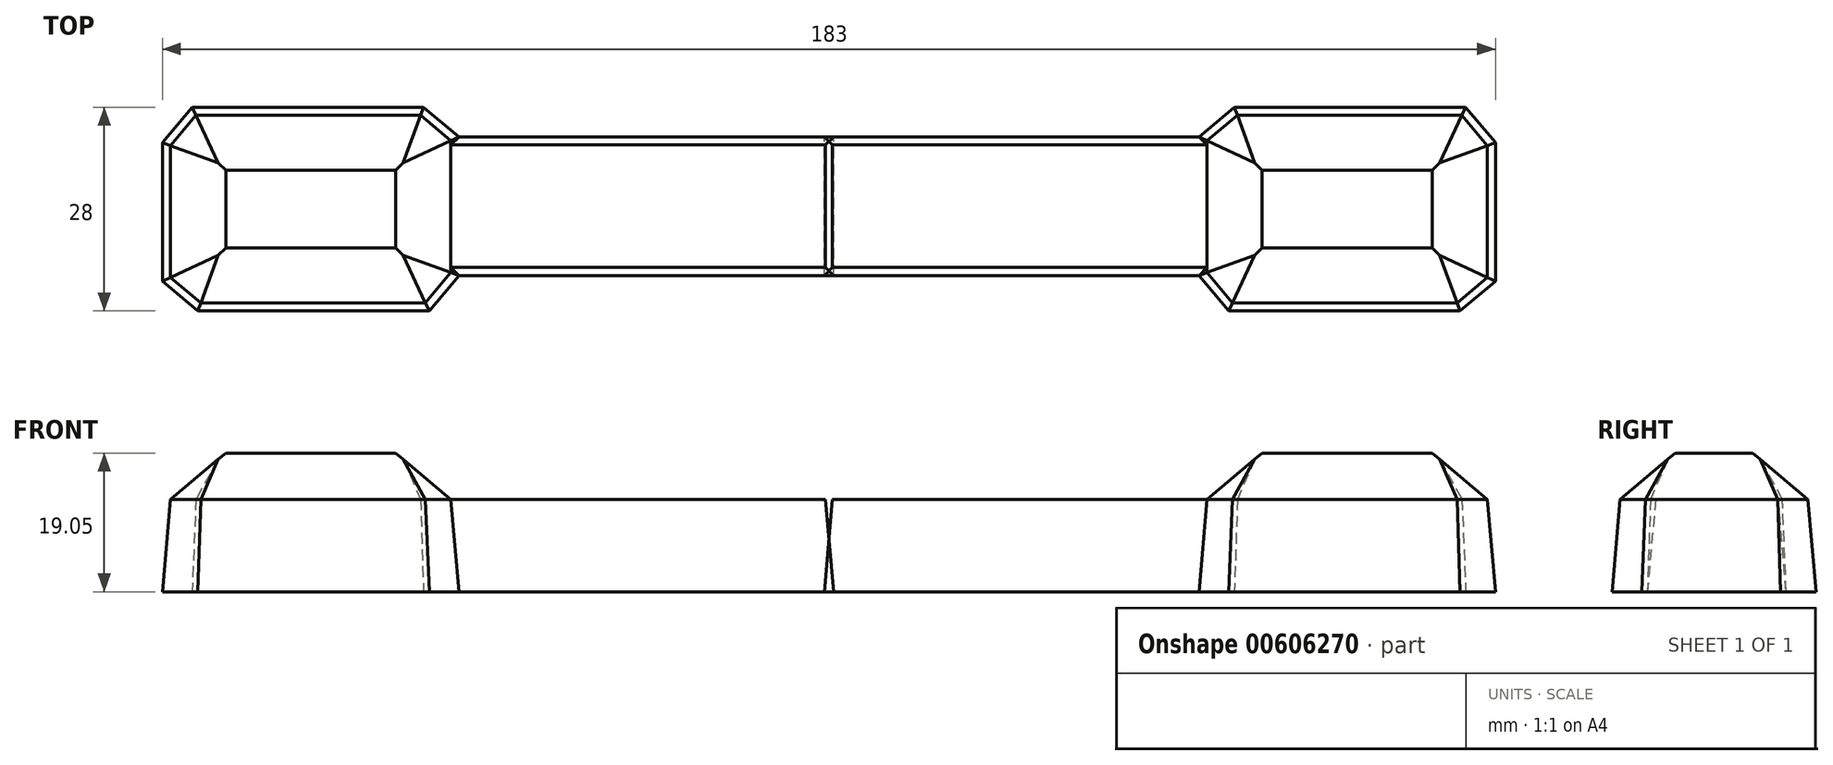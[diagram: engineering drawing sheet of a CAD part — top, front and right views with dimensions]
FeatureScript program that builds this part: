
annotation { "Feature Type Name" : "Feature", "Feature Type Description" : "" }
export const myFeature = defineFeature(function(context is Context, id is Id, definition is map)
    precondition{}
    {
        {
            var Q0;
            Q0=qCreatedBy(makeId("Top.planeOp"),FACE);
            var sketch = newSketch(context, id + "F0", { "sketchPlane" : qUnion([Q0])});
            skPoint(sketch, "E0.middle", {"position": v(0, 0) * mm});
            skLineSegment(sketch, "E1", {"start": v(50.8, 9.53) * mm, "end": v(50.8, -9.52) * mm});
            skLineSegment(sketch, "E2", {"start": v(50.8, 9.52) * mm, "end": v(55.66, 13.6) * mm});
            skLineSegment(sketch, "E3", {"start": v(50.8, -9.52) * mm, "end": v(54.88, -14.39) * mm});
            skLineSegment(sketch, "E4", {"start": v(54.88, -14.39) * mm, "end": v(86.63, -14.39) * mm});
            skLineSegment(sketch, "E5", {"start": v(55.66, 13.6) * mm, "end": v(87.41, 13.6) * mm});
            skLineSegment(sketch, "E6", {"start": v(87.41, 13.6) * mm, "end": v(91.5, 8.74) * mm});
            skLineSegment(sketch, "E7", {"start": v(86.63, -14.39) * mm, "end": v(91.5, -10.3) * mm});
            skLineSegment(sketch, "E8", {"start": v(91.5, 8.74) * mm, "end": v(91.5, -10.3) * mm});
            skLineSegment(sketch, "E9", {"start": v(50.8, 9.53) * mm, "end": v(57.13, 9.53) * mm});
            skLineSegment(sketch, "E10", {"start": v(57.13, 9.53) * mm, "end": v(57.13, -9.53) * mm});
            skLineSegment(sketch, "E11", {"start": v(57.13, -9.53) * mm, "end": v(50.8, -9.53) * mm});
            skLineSegment(sketch, "E12", {"start": v(-0.62, 9.53) * mm, "end": v(-0.62, -9.53) * mm});
            skLineSegment(sketch, "E13", {"start": v(-0.62, 9.53) * mm, "end": v(50.8, 9.53) * mm});
            skLineSegment(sketch, "E14", {"start": v(-0.62, -9.52) * mm, "end": v(50.8, -9.52) * mm});
            skSolve(sketch);
        }
        {
            var Q0;
            Q0=makeQuery(id+"F0.imprint","IMPRINT",FACE,{"disambiguationData":[TD([[makeQuery(id+"F0.imprint","IMPRINT",EDGE,{"derivedFrom":sQuery(id+"F0.wireOp",EDGE,"LX4vih2L-8PL2-zWTP-tvqg-00dXrwP9e0R8")}),-1.0]])]});
            var Q1;
            Q1=makeQuery(id+"F0.imprint","IMPRINT",FACE,{"disambiguationData":[TD([[makeQuery(id+"F0.imprint","IMPRINT",EDGE,{"derivedFrom":sQuery(id+"F0.wireOp",EDGE,"E1")}),1.0]])]});
            var Q2;
            Q2=makeQuery(id+"F0.imprint","IMPRINT",FACE,{"disambiguationData":[TD([[makeQuery(id+"F0.imprint","IMPRINT",EDGE,{"derivedFrom":sQuery(id+"F0.wireOp",EDGE,"E1")}),-1.0]])]});
            extrude(context, id + "F1", {"entities" : qUnion([Q0, Q1, Q2]), "depth" : 12.7 * mm, "offsetDistance" : 25.4 * mm, "hasDraft" : true, "draftAngle" : 5 * degree, "draftPullDirection" : true});
        }
        {
            var Q0;
            Q0=makeQuery(id+"F0.imprint","IMPRINT",FACE,{"disambiguationData":[TD([[makeQuery(id+"F0.imprint","IMPRINT",EDGE,{"derivedFrom":sQuery(id+"F0.wireOp",EDGE,"E1")}),1.0]])]});
            var Q1;
            Q1=makeQuery(id+"F0.imprint","IMPRINT",FACE,{"disambiguationData":[TD([[makeQuery(id+"F0.imprint","IMPRINT",EDGE,{"derivedFrom":sQuery(id+"F0.wireOp",EDGE,"E2")}),-1.0]])]});
            extrude(context, id + "F2", {"entities" : qUnion([Q0, Q1]), "operationType" : NewBodyOperationType.ADD, "depth" : 12.7 * mm, "offsetDistance" : 25.4 * mm, "hasDraft" : true, "draftAngle" : 5 * degree, "draftPullDirection" : true});
        }
        {
            var Q0;
            Q0=makeQuery(id+"F2.boolean.opBoolean","MERGE",FACE,{"derivedFrom":[makeQuery(id+"F1.opExtrude","CAP_FACE",FACE,{"disambiguationData":[OSD([sQuery(id+"F0.wireOp",EDGE,"LX4vih2L-8PL2-zWTP-tvqg-00dXrwP9e0R8"),sQuery(id+"F0.wireOp",EDGE,"2FfLaITP-Q9AS-mCcM-fKqD-aldsRTrWUq4b"),sQuery(id+"F0.wireOp",EDGE,"0Gyn5qcO-PV2c-2Bck-4XNA-dSiD7LYEdiYG"),sQuery(id+"F0.wireOp",EDGE,"E9"),sQuery(id+"F0.wireOp",EDGE,"E10"),sQuery(id+"F0.wireOp",EDGE,"E11")])],"isStart":false}),makeQuery(id+"F2.opExtrude","CAP_FACE",FACE,{"disambiguationData":[OSD([sQuery(id+"F0.wireOp",EDGE,"E1"),sQuery(id+"F0.wireOp",EDGE,"E2"),sQuery(id+"F0.wireOp",EDGE,"E3"),sQuery(id+"F0.wireOp",EDGE,"E4"),sQuery(id+"F0.wireOp",EDGE,"E5"),sQuery(id+"F0.wireOp",EDGE,"E6"),sQuery(id+"F0.wireOp",EDGE,"E7"),sQuery(id+"F0.wireOp",EDGE,"E8")])],"isStart":false})]});
            var sketch = newSketch(context, id + "F3", { "sketchPlane" : qUnion([Q0])});
            skLineSegment(sketch, "E15", {"start": v(51.91, 8.41) * mm, "end": v(51.91, -8.41) * mm});
            skSolve(sketch);
        }
        {
            var Q0;
            Q0=makeQuery(id+"F3.imprint","IMPRINT",FACE,{"disambiguationData":[TD([[makeQuery(id+"F3.imprint","IMPRINT",EDGE,{"derivedFrom":sQuery(id+"F3.wireOp",EDGE,"E15")}),1.0]])]});
            extrude(context, id + "F4", {"entities" : qUnion([Q0]), "operationType" : NewBodyOperationType.ADD, "depth" : 6.35 * mm, "offsetDistance" : 25.4 * mm, "hasDraft" : true, "draftAngle" : 50 * degree, "draftPullDirection" : true});
        }
        {
            var Q0;
            Q0=makeQuery(id+"F1.opExtrude","SWEPT_BODY",BODY,{"disambiguationData":[OSD([sQuery(id+"F0.wireOp",EDGE,"LX4vih2L-8PL2-zWTP-tvqg-00dXrwP9e0R8"),sQuery(id+"F0.wireOp",EDGE,"2FfLaITP-Q9AS-mCcM-fKqD-aldsRTrWUq4b"),sQuery(id+"F0.wireOp",EDGE,"0Gyn5qcO-PV2c-2Bck-4XNA-dSiD7LYEdiYG"),sQuery(id+"F0.wireOp",EDGE,"E9"),sQuery(id+"F0.wireOp",EDGE,"E10"),sQuery(id+"F0.wireOp",EDGE,"E11")])]});
            var Q1;
            Q1=qCreatedBy(makeId("Right.planeOp"),FACE);
            mirror(context, id + "F5", {"entities" : qUnion([Q0]), "mirrorPlane" : qUnion([Q1])});
        }
    });
